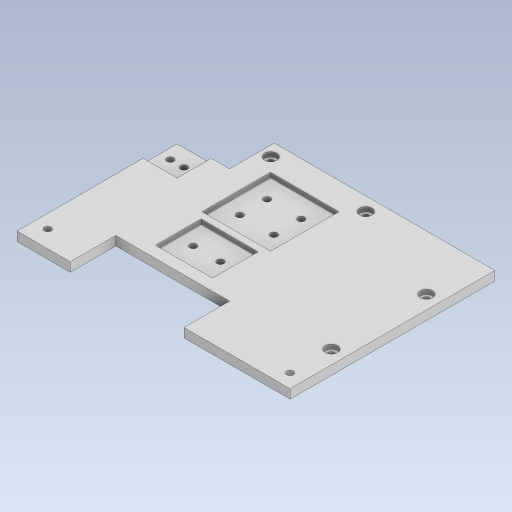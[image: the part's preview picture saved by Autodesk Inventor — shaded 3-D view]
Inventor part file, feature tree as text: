
AUTODESK INVENTOR PART (.ipt)
format: ipt  version: 2023.5 (Build 275446000, 446)  size: 412,160 bytes
history: native  units: in
note: dims shown in document units (in); Inventor stores cm internally (conversion verified against a paired STEP export)
features: extrude x2, sketch x1
ambient origin geometry x8: Origin, YZ Plane, XZ Plane, XY Plane, X Axis, Y Axis, Z Axis, Center Point
bodies: Body1 (feature_tree)
feature tree (3):
  sketch  "Sketch1"  dims[d0=4.7244in d1=3.5433in d21=0.1181in d22=0.2559in d23=0.1181in d24=0.2559in d25=0.1181in d27=0.1181in d32=0.1969in d38=0.1181in d39=0.2165in d40=0.2362in d41=0.2165in d42=0.1181in d43=0.2362in d44=0.2362in d45=0.1181in d46=0.2362in d59=0.7736in d60=0.1181in d61=0.1969in d63=0.2953in d64=0.1575in d65=0.0in d66=0.0787in d67=0.0in d68=0.1181in d69=0.1181in d70=0.8219in d71=0.8219in d72=0.2165in d73=0.2165in d74=0.0in d75=0.0in d76=0.2953in d77=0.2953in d78=0.2953in d79=0.2953in d81=0.315in d33=0.0197in d34=0.0344in d35=0.0197in d36=0.0344in]
  extrude  "Extrusion3"  Depth=3.5433in
  extrude  "Extrusion4"  Depth=0.1181in
